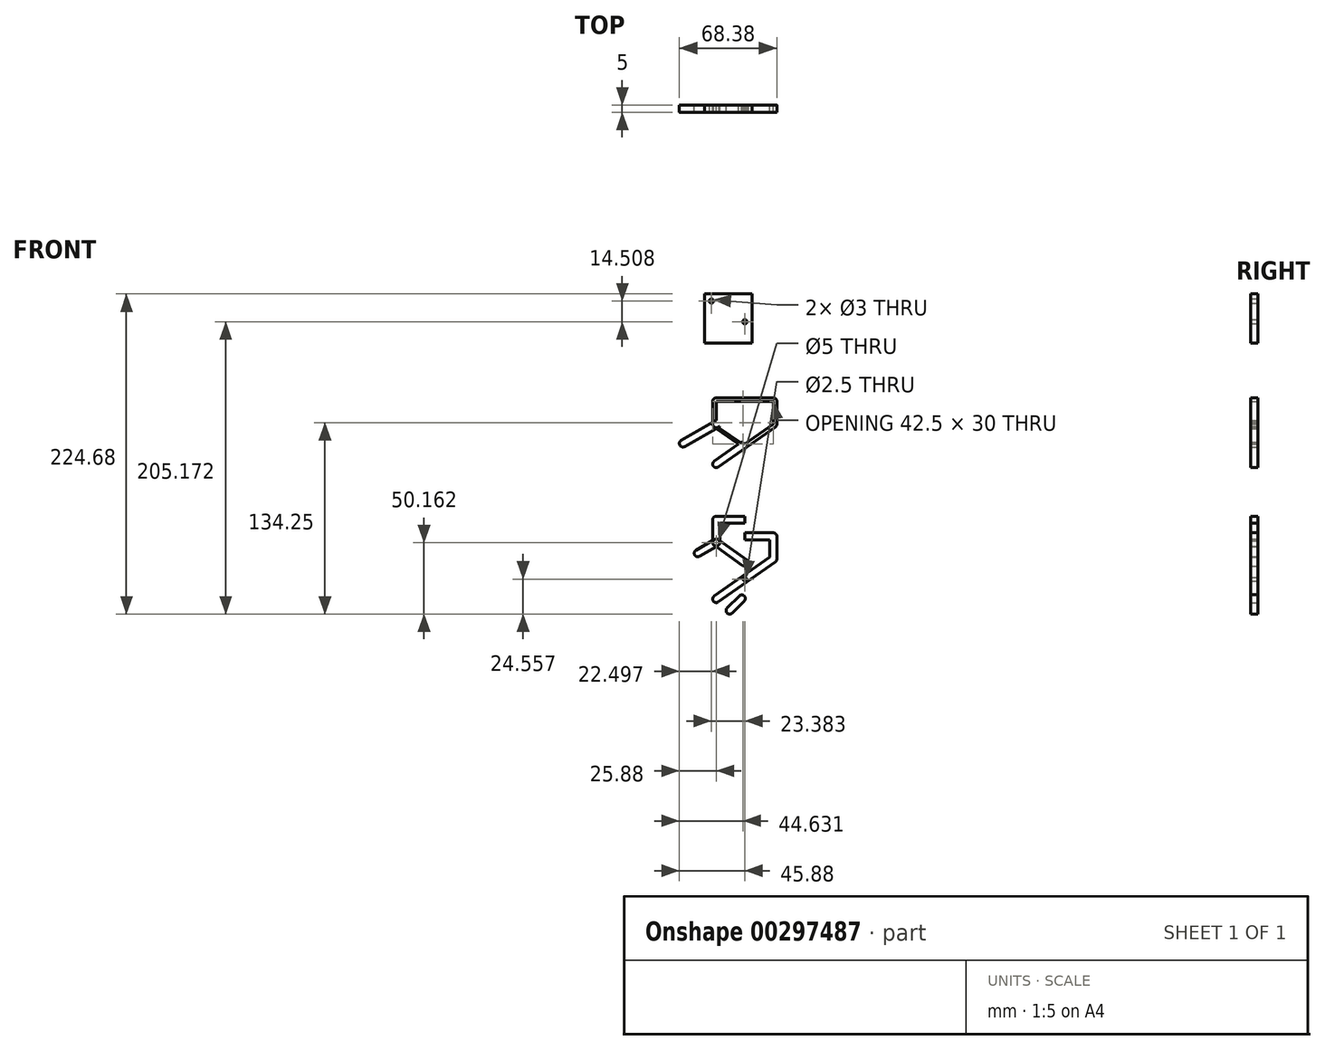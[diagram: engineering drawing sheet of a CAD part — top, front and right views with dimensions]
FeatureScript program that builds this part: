
annotation { "Feature Type Name" : "Feature", "Feature Type Description" : "" }
export const myFeature = defineFeature(function(context is Context, id is Id, definition is map)
    precondition{}
    {
        {
            var Q0;
            Q0=qCreatedBy(makeId("Front.planeOp"),FACE);
            var sketch = newSketch(context, id + "F0", { "sketchPlane" : qUnion([Q0])});
            skLineSegment(sketch, "E0", {"start": v(0, 0) * mm, "end": v(20, 0) * mm});
            skLineSegment(sketch, "E1", {"start": v(20, 0) * mm, "end": v(20, -16) * mm});
            skLineSegment(sketch, "E2", {"start": v(20, -16) * mm, "end": v(-20, -44) * mm});
            skLineSegment(sketch, "E3", {"start": v(0, -30) * mm, "end": v(-20, -16) * mm});
            skLineSegment(sketch, "E4", {"start": v(-20, -16) * mm, "end": v(-20, 0) * mm});
            skLineSegment(sketch, "E5", {"start": v(-20, 0) * mm, "end": v(0, 0) * mm});
            skArc(sketch, "E6.0.startCap", {"start": v(18.57, -13.95) * mm, "mid": v(22.05, -14.56) * mm, "end": v(21.43, -18.04) * mm});
            skArc(sketch, "E6.0.endCap", {"start": v(-18.57, -46.05) * mm, "mid": v(-22.05, -45.44) * mm, "end": v(-21.43, -41.96) * mm});
            skLineSegment(sketch, "E6.0.left", {"start": v(21.43, -18.04) * mm, "end": v(-18.57, -46.05) * mm});
            skLineSegment(sketch, "E6.0.right", {"start": v(18.57, -13.95) * mm, "end": v(-21.43, -41.96) * mm});
            skArc(sketch, "E7.0.startCap", {"start": v(17.5, 0) * mm, "mid": v(20, 2.5) * mm, "end": v(22.5, 0) * mm});
            skArc(sketch, "E7.0.endCap", {"start": v(22.5, -16) * mm, "mid": v(20, -18.5) * mm, "end": v(17.5, -16) * mm});
            skLineSegment(sketch, "E7.0.left", {"start": v(22.5, 0) * mm, "end": v(22.5, -16) * mm});
            skLineSegment(sketch, "E7.0.right", {"start": v(17.5, 0) * mm, "end": v(17.5, -16) * mm});
            skArc(sketch, "E8.0.endCap", {"start": v(20, 2.5) * mm, "mid": v(22.5, 0) * mm, "end": v(20, -2.5) * mm});
            skLineSegment(sketch, "E8.0.left", {"start": v(0, 2.5) * mm, "end": v(20, 2.5) * mm});
            skLineSegment(sketch, "E8.0.right", {"start": v(0, -2.5) * mm, "end": v(20, -2.5) * mm});
            skArc(sketch, "E8.1.startCap", {"start": v(-20, -2.5) * mm, "mid": v(-22.5, 0) * mm, "end": v(-20, 2.5) * mm});
            skLineSegment(sketch, "E8.1.left", {"start": v(-20, 2.5) * mm, "end": v(0, 2.5) * mm});
            skLineSegment(sketch, "E8.1.right", {"start": v(-20, -2.5) * mm, "end": v(0, -2.5) * mm});
            skArc(sketch, "E8.2.startCap", {"start": v(-17.5, -16) * mm, "mid": v(-20, -18.5) * mm, "end": v(-22.5, -16) * mm});
            skArc(sketch, "E8.2.endCap", {"start": v(-22.5, 0) * mm, "mid": v(-20, 2.5) * mm, "end": v(-17.5, 0) * mm});
            skLineSegment(sketch, "E8.2.left", {"start": v(-22.5, -16) * mm, "end": v(-22.5, 0) * mm});
            skLineSegment(sketch, "E8.2.right", {"start": v(-17.5, -16) * mm, "end": v(-17.5, 0) * mm});
            skArc(sketch, "E8.3.startCap", {"start": v(1.43, -27.95) * mm, "mid": v(2.05, -31.43) * mm, "end": v(-1.43, -32.05) * mm});
            skArc(sketch, "E8.3.endCap", {"start": v(-21.43, -18.04) * mm, "mid": v(-22.05, -14.56) * mm, "end": v(-18.57, -13.95) * mm});
            skLineSegment(sketch, "E8.3.left", {"start": v(-1.43, -32.05) * mm, "end": v(-21.43, -18.04) * mm});
            skLineSegment(sketch, "E8.3.right", {"start": v(1.43, -27.95) * mm, "end": v(-18.57, -13.95) * mm});
            skLineSegment(sketch, "E9", {"start": v(-16.93, -18.15) * mm, "end": v(-3, -27.9) * mm});
            skArc(sketch, "E10.0.startCap", {"start": v(-17.5, -18.97) * mm, "mid": v(-17.74, -17.58) * mm, "end": v(-16.35, -17.33) * mm});
            skArc(sketch, "E10.0.endCap", {"start": v(-2.43, -27.08) * mm, "mid": v(-2.18, -28.47) * mm, "end": v(-3.57, -28.72) * mm});
            skLineSegment(sketch, "E10.0.left", {"start": v(-16.35, -17.33) * mm, "end": v(-2.43, -27.08) * mm});
            skLineSegment(sketch, "E10.0.right", {"start": v(-17.5, -18.97) * mm, "end": v(-3.57, -28.72) * mm});
            skLineSegment(sketch, "E11", {"start": v(0, 2.5) * mm, "end": v(0, -2.5) * mm});
            skLineSegment(sketch, "E12", {"start": v(-20, -16) * mm, "end": v(-33, -23.5) * mm});
            skArc(sketch, "E13.0.startCap", {"start": v(-21.25, -13.83) * mm, "mid": v(-17.83, -14.75) * mm, "end": v(-18.75, -18.16) * mm});
            skArc(sketch, "E13.0.endCap", {"start": v(-31.74, -25.66) * mm, "mid": v(-35.16, -24.75) * mm, "end": v(-34.24, -21.33) * mm});
            skLineSegment(sketch, "E13.0.left", {"start": v(-18.75, -18.16) * mm, "end": v(-31.74, -25.66) * mm});
            skLineSegment(sketch, "E13.0.right", {"start": v(-21.25, -13.83) * mm, "end": v(-34.24, -21.33) * mm});
            skLineSegment(sketch, "E14", {"start": v(-33, -23.5) * mm, "end": v(-43.38, -29.5) * mm});
            skArc(sketch, "E15.0.startCap", {"start": v(-34.24, -21.33) * mm, "mid": v(-30.83, -22.25) * mm, "end": v(-31.74, -25.66) * mm});
            skArc(sketch, "E15.0.endCap", {"start": v(-42.13, -31.66) * mm, "mid": v(-45.55, -30.75) * mm, "end": v(-44.63, -27.33) * mm});
            skLineSegment(sketch, "E15.0.left", {"start": v(-31.74, -25.66) * mm, "end": v(-42.13, -31.66) * mm});
            skLineSegment(sketch, "E15.0.right", {"start": v(-34.24, -21.33) * mm, "end": v(-44.63, -27.33) * mm});
            skLineSegment(sketch, "E16", {"start": v(0, -113.1) * mm, "end": v(-20, -99.09) * mm});
            skLineSegment(sketch, "E17", {"start": v(-20, -99.09) * mm, "end": v(-20, -83.1) * mm});
            skLineSegment(sketch, "E18", {"start": v(-20, -83.1) * mm, "end": v(0, -83.1) * mm});
            skArc(sketch, "E19.1.startCap", {"start": v(-20, -85.6) * mm, "mid": v(-22.5, -83.1) * mm, "end": v(-20, -80.6) * mm});
            skLineSegment(sketch, "E19.1.left", {"start": v(-20, -80.6) * mm, "end": v(0, -80.6) * mm});
            skLineSegment(sketch, "E19.1.right", {"start": v(-20, -85.6) * mm, "end": v(0, -85.6) * mm});
            skArc(sketch, "E19.2.startCap", {"start": v(-17.5, -99.09) * mm, "mid": v(-20, -101.59) * mm, "end": v(-22.5, -99.09) * mm});
            skArc(sketch, "E19.2.endCap", {"start": v(-22.5, -83.1) * mm, "mid": v(-20, -80.6) * mm, "end": v(-17.5, -83.1) * mm});
            skLineSegment(sketch, "E19.2.left", {"start": v(-22.5, -99.09) * mm, "end": v(-22.5, -83.1) * mm});
            skLineSegment(sketch, "E19.2.right", {"start": v(-17.5, -99.09) * mm, "end": v(-17.5, -83.1) * mm});
            skArc(sketch, "E19.3.startCap", {"start": v(1.43, -111.04) * mm, "mid": v(2.05, -114.53) * mm, "end": v(-1.43, -115.14) * mm});
            skArc(sketch, "E19.3.endCap", {"start": v(-21.43, -101.14) * mm, "mid": v(-22.05, -97.65) * mm, "end": v(-18.57, -97.04) * mm});
            skLineSegment(sketch, "E19.3.left", {"start": v(-1.43, -115.14) * mm, "end": v(-21.43, -101.14) * mm});
            skLineSegment(sketch, "E19.3.right", {"start": v(1.43, -111.04) * mm, "end": v(-18.57, -97.04) * mm});
            skLineSegment(sketch, "E20", {"start": v(0, -80.6) * mm, "end": v(0, -85.6) * mm});
            skLineSegment(sketch, "E21", {"start": v(-20, -99.09) * mm, "end": v(-33, -106.59) * mm});
            skArc(sketch, "E22.0.startCap", {"start": v(-21.25, -96.92) * mm, "mid": v(-17.83, -97.84) * mm, "end": v(-18.75, -101.25) * mm});
            skArc(sketch, "E22.0.endCap", {"start": v(-31.74, -108.75) * mm, "mid": v(-35.16, -107.84) * mm, "end": v(-34.24, -104.42) * mm});
            skLineSegment(sketch, "E22.0.left", {"start": v(-18.75, -101.25) * mm, "end": v(-31.74, -108.75) * mm});
            skLineSegment(sketch, "E22.0.right", {"start": v(-21.25, -96.92) * mm, "end": v(-34.24, -104.42) * mm});
            skLineSegment(sketch, "E23", {"start": v(0, -94.7) * mm, "end": v(20, -94.7) * mm});
            skLineSegment(sketch, "E24", {"start": v(20, -94.7) * mm, "end": v(20, -110.69) * mm});
            skLineSegment(sketch, "E25", {"start": v(20, -110.69) * mm, "end": v(-20, -138.7) * mm});
            skArc(sketch, "E26.0.startCap", {"start": v(18.57, -108.64) * mm, "mid": v(22.05, -109.25) * mm, "end": v(21.43, -112.74) * mm});
            skArc(sketch, "E26.0.endCap", {"start": v(-18.57, -140.74) * mm, "mid": v(-22.05, -140.13) * mm, "end": v(-21.43, -136.65) * mm});
            skLineSegment(sketch, "E26.0.left", {"start": v(21.43, -112.74) * mm, "end": v(-18.57, -140.74) * mm});
            skLineSegment(sketch, "E26.0.right", {"start": v(18.57, -108.64) * mm, "end": v(-21.43, -136.65) * mm});
            skArc(sketch, "E27.0.startCap", {"start": v(17.5, -94.7) * mm, "mid": v(20, -92.2) * mm, "end": v(22.5, -94.7) * mm});
            skArc(sketch, "E27.0.endCap", {"start": v(22.5, -110.69) * mm, "mid": v(20, -113.19) * mm, "end": v(17.5, -110.69) * mm});
            skLineSegment(sketch, "E27.0.left", {"start": v(22.5, -94.7) * mm, "end": v(22.5, -110.69) * mm});
            skLineSegment(sketch, "E27.0.right", {"start": v(17.5, -94.7) * mm, "end": v(17.5, -110.69) * mm});
            skArc(sketch, "E28.0.endCap", {"start": v(20, -92.2) * mm, "mid": v(22.5, -94.7) * mm, "end": v(20, -97.2) * mm});
            skLineSegment(sketch, "E28.0.left", {"start": v(0, -92.2) * mm, "end": v(20, -92.2) * mm});
            skLineSegment(sketch, "E28.0.right", {"start": v(0, -97.2) * mm, "end": v(20, -97.2) * mm});
            skLineSegment(sketch, "E29", {"start": v(0, -92.2) * mm, "end": v(0, -97.2) * mm});
            skLineSegment(sketch, "E30", {"start": v(-2.12, -138.27) * mm, "end": v(-10.6, -146.75) * mm});
            skArc(sketch, "E31.0.startCap", {"start": v(-3.89, -136.5) * mm, "mid": v(-0.35, -136.5) * mm, "end": v(-0.35, -140.03) * mm});
            skArc(sketch, "E31.0.endCap", {"start": v(-8.84, -148.52) * mm, "mid": v(-12.37, -148.52) * mm, "end": v(-12.37, -144.98) * mm});
            skLineSegment(sketch, "E31.0.left", {"start": v(-0.35, -140.03) * mm, "end": v(-8.84, -148.52) * mm});
            skLineSegment(sketch, "E31.0.right", {"start": v(-3.89, -136.5) * mm, "end": v(-12.37, -144.98) * mm});
            skPoint(sketch, "E32", {"position": v(0, 55.92) * mm});
            skLineSegment(sketch, "E33.bottom", {"start": v(-28.38, 75.43) * mm, "end": v(5, 75.43) * mm});
            skLineSegment(sketch, "E33.top", {"start": v(-28.38, 40.92) * mm, "end": v(5, 40.92) * mm});
            skLineSegment(sketch, "E33.left", {"start": v(-28.38, 75.43) * mm, "end": v(-28.38, 40.92) * mm});
            skLineSegment(sketch, "E33.right", {"start": v(5, 75.43) * mm, "end": v(5, 40.92) * mm});
            skCircle(sketch, "E34", {"center": v(-23.38, 70.43) * mm, "radius": 1.5 * mm});
            skCircle(sketch, "E35", {"center": v(0, 55.92) * mm, "radius": 1.5 * mm});
            skPoint(sketch, "E36", {"position": v(0, -124.7) * mm});
            skCircle(sketch, "E37", {"center": v(0, -124.7) * mm, "radius": 1.25 * mm});
            skSolve(sketch);
        }
        {
            var Q0;
            Q0 = qSketchRegion(id + "F0", true);
            var Q1;
            {var subQ5=sQuery(id+"F0.wireOp",EDGE,"E19.2.startCap");Q1=makeQuery(id+"F0.imprint","IMPRINT",FACE,{"disambiguationData":[TD([[makeQuery(id+"F0.imprint","IMPRINT",EDGE,{"derivedFrom":subQ5}),-1.0]])]});}
            var Q2;
            {var subQ3=sQuery(id+"F0.wireOp",EDGE,"E19.3.endCap");var subQ5=makeQuery(id+"F0.imprint","INTERSECT",VERTEX,{"derivedFrom":[sQuery(id+"F0.wireOp",EDGE,"E19.2.left"),subQ3]});Q2=makeQuery(id+"F0.imprint","IMPRINT",FACE,{"disambiguationData":[TD([[makeQuery(id+"F0.imprint","IMPRINT",EDGE,{"disambiguationData":[TD([[subQ5,1.0]])],"derivedFrom":subQ3}),-1.0]])]});}
            var Q3;
            {var subQ0=sQuery(id+"F0.wireOp",EDGE,"E22.0.startCap");var subQ2=makeQuery(id+"F0.imprint","INTERSECT",VERTEX,{"derivedFrom":[sQuery(id+"F0.wireOp",EDGE,"E19.3.right"),subQ0]});Q3=makeQuery(id+"F0.imprint","IMPRINT",FACE,{"disambiguationData":[TD([[makeQuery(id+"F0.imprint","IMPRINT",EDGE,{"disambiguationData":[TD([[subQ2,1.0]])],"derivedFrom":subQ0}),-1.0]])]});}
            extrude(context, id + "F1", {"entities" : qUnion([Q0, Q1, Q2, Q3]), "depth" : 5 * mm});
        }
    });
